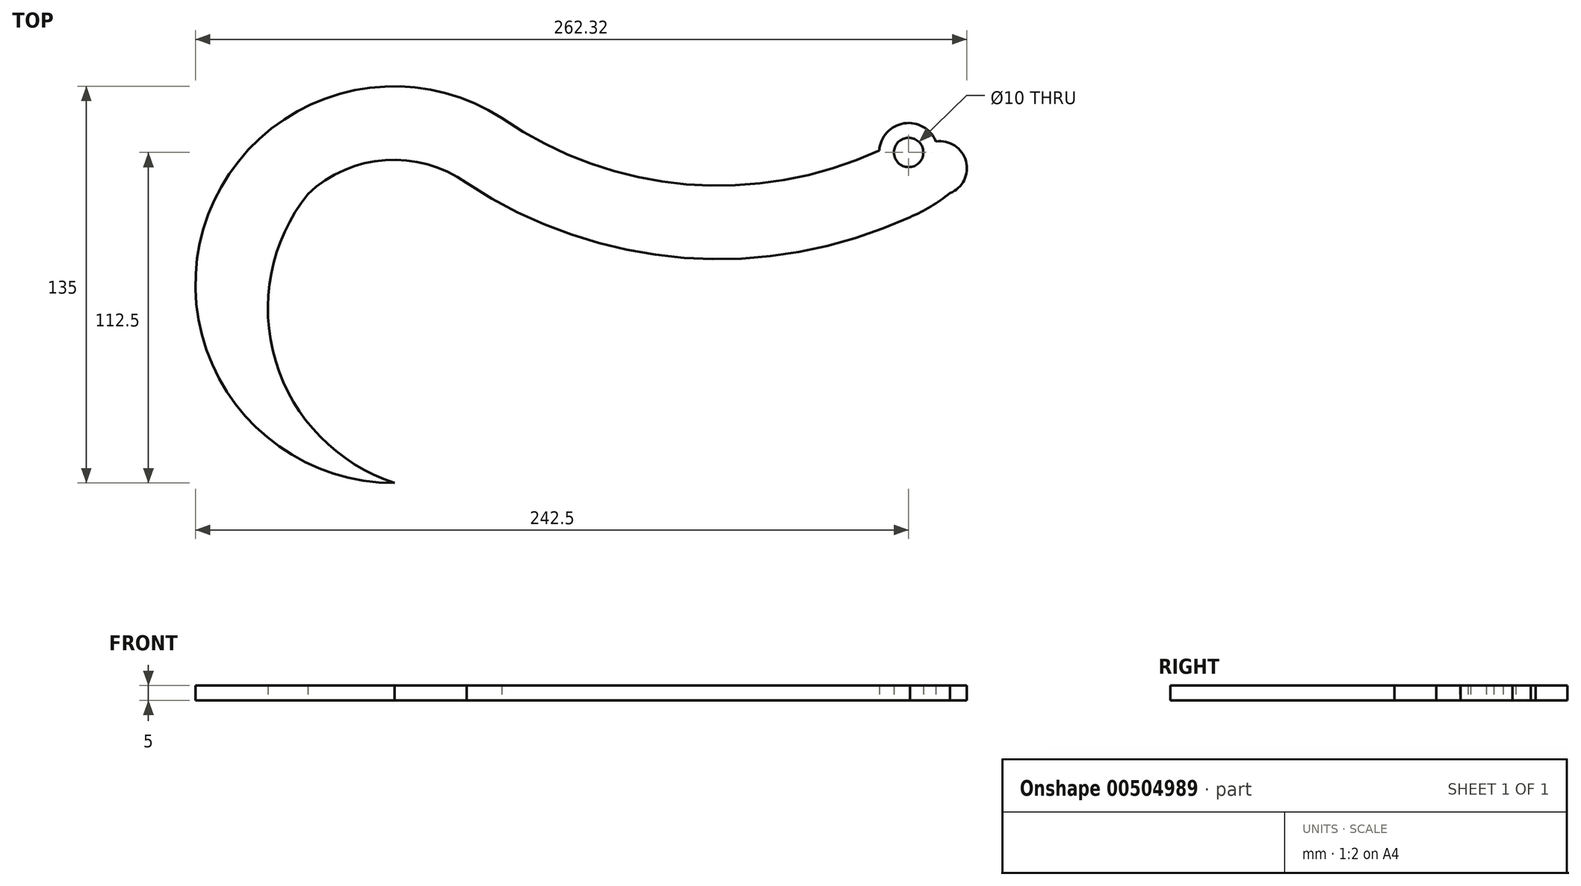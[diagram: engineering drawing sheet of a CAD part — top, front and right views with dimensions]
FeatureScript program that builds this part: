
annotation { "Feature Type Name" : "Feature", "Feature Type Description" : "" }
export const myFeature = defineFeature(function(context is Context, id is Id, definition is map)
    precondition{}
    {
        {
            var Q0;
            Q0=qCreatedBy(makeId("Top.planeOp"),FACE);
            var sketch = newSketch(context, id + "F0", { "sketchPlane" : qUnion([Q0])});
            skArc(sketch, "E0", {"start": v(36.68, 56.67) * mm, "mid": v(-64.76, 19.02) * mm, "end": v(0.2, -67.5) * mm});
            skCircle(sketch, "E1", {"center": v(175, 45) * mm, "radius": 5 * mm});
            skArc(sketch, "E2", {"start": v(184.29, 48.7) * mm, "mid": v(173.45, 54.88) * mm, "end": v(165.02, 45.68) * mm});
            skArc(sketch, "E3", {"start": v(36.68, 56.67) * mm, "mid": v(99.4, 34.16) * mm, "end": v(165.02, 45.68) * mm});
            skArc(sketch, "E4.0", {"start": v(24.7, 34.58) * mm, "mid": v(98.6, 9.14) * mm, "end": v(175.51, 22.98) * mm});
            skArc(sketch, "E5", {"start": v(24.7, 34.58) * mm, "mid": v(-2.96, 42.4) * mm, "end": v(-29.27, 30.81) * mm});
            skArc(sketch, "E6", {"start": v(175.51, 22.98) * mm, "mid": v(182.54, 26.6) * mm, "end": v(189.02, 31.14) * mm});
            skArc(sketch, "E7", {"start": v(-29.27, 30.81) * mm, "mid": v(-40.23, -26.05) * mm, "end": v(0.2, -67.5) * mm});
            skArc(sketch, "E8", {"start": v(189.02, 31.14) * mm, "mid": v(194.51, 42.03) * mm, "end": v(184.29, 48.7) * mm});
            skSolve(sketch);
        }
        {
            var Q0;
            Q0 = qSketchRegion(id + "F0", true);
            extrude(context, id + "F1", {"entities" : qUnion([Q0]), "depth" : 5 * mm});
        }
    });
